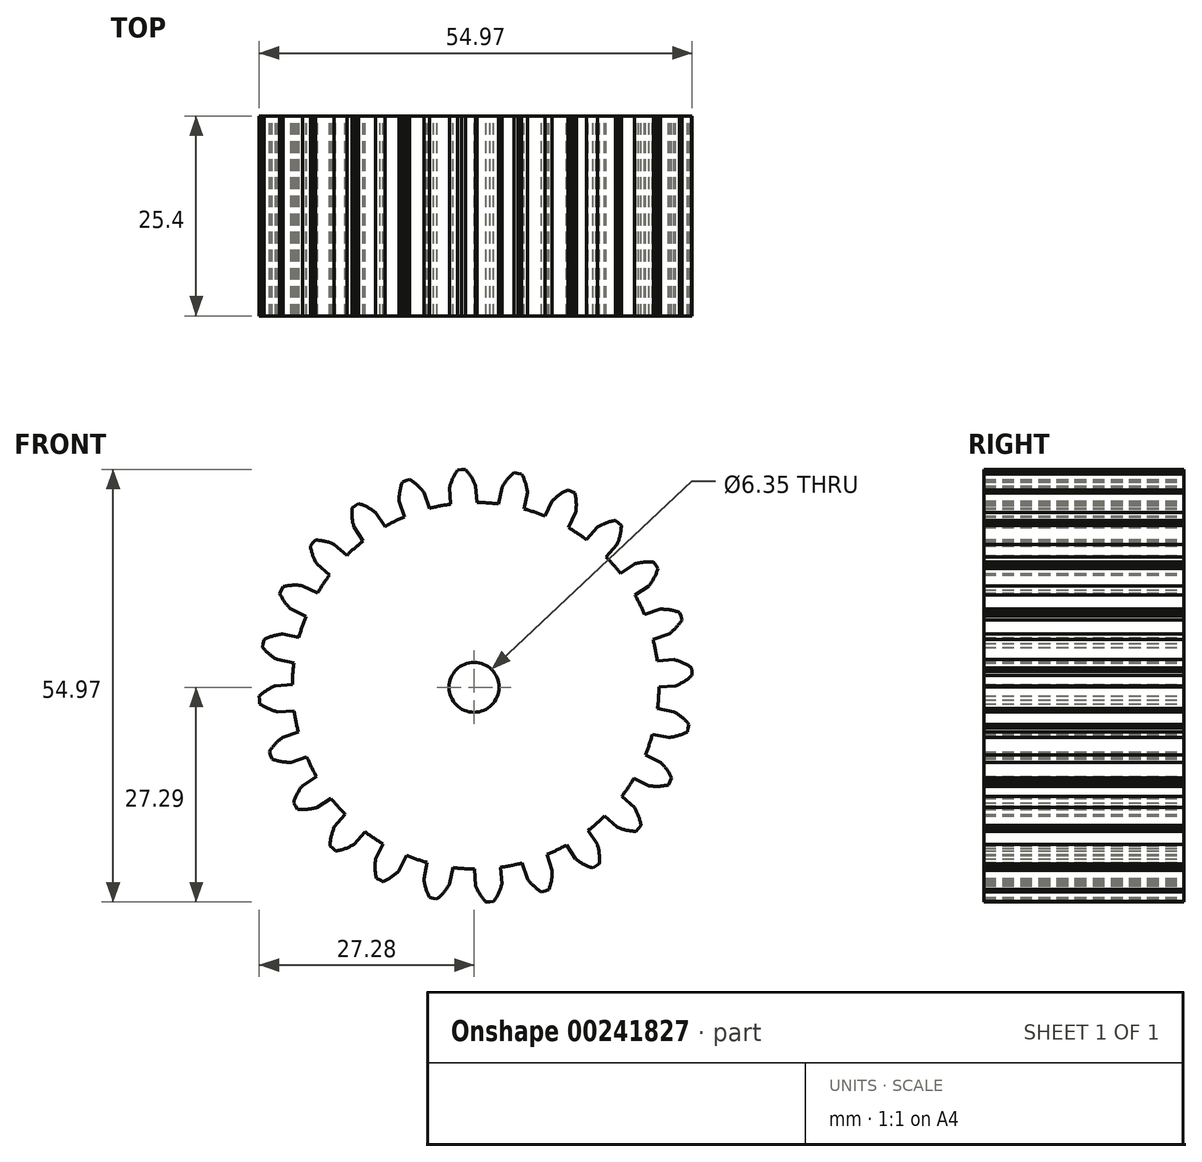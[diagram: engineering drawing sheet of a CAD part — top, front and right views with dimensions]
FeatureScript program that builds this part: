
annotation { "Feature Type Name" : "Feature", "Feature Type Description" : "" }
export const myFeature = defineFeature(function(context is Context, id is Id, definition is map)
    precondition{}
    {
        {
            var Q0;
            Q0=qCreatedBy(makeId("Front.planeOp"),FACE);
            var sketch = newSketch(context, id + "F0", { "sketchPlane" : qUnion([Q0])});
            skCircle(sketch, "E0", {"center": v(0.2, 0.2) * mm, "radius": 23.28 * mm});
            skArc(sketch, "E1.trimOffspring", {"start": v(0.2, 25.6) * mm, "mid": v(-0.35, 26.7) * mm, "end": v(-1.1, 27.68) * mm});
            skLineSegment(sketch, "E2", {"start": v(0.2, 25.6) * mm, "end": v(0.35, 23.48) * mm});
            skLineSegment(sketch, "E3", {"start": v(-1.1, 27.68) * mm, "end": v(-1.6, 27.66) * mm});
            skLineSegment(sketch, "E4.MirrorCS", {"start": v(-2.08, 27.61) * mm, "end": v(-1.6, 27.66) * mm});
            skArc(sketch, "E5.MirrorCS", {"start": v(-3.1, 25.38) * mm, "mid": v(-2.7, 26.55) * mm, "end": v(-2.08, 27.61) * mm});
            skLineSegment(sketch, "E6.MirrorCS", {"start": v(-3.1, 25.38) * mm, "end": v(-2.97, 23.26) * mm});
            skPoint(sketch, "E7.orphan", {"position": v(-2.8, 20.76) * mm});
            skPoint(sketch, "E8.orphan", {"position": v(0.51, 20.98) * mm});
            skLineSegment(sketch, "E9.1.0", {"start": v(-9.51, 23.66) * mm, "end": v(-8.83, 21.65) * mm});
            skArc(sketch, "E9.1.1", {"start": v(-9.51, 23.66) * mm, "mid": v(-9.42, 24.9) * mm, "end": v(-9.1, 26.09) * mm});
            skLineSegment(sketch, "E9.1.2", {"start": v(-9.1, 26.09) * mm, "end": v(-8.64, 26.25) * mm});
            skLineSegment(sketch, "E9.1.3", {"start": v(-8.17, 26.4) * mm, "end": v(-8.64, 26.25) * mm});
            skArc(sketch, "E9.1.4", {"start": v(-6.37, 24.73) * mm, "mid": v(-7.19, 25.65) * mm, "end": v(-8.17, 26.4) * mm});
            skLineSegment(sketch, "E9.1.5", {"start": v(-6.37, 24.73) * mm, "end": v(-5.68, 22.72) * mm});
            skLineSegment(sketch, "E9.2.0", {"start": v(-15.25, 20.35) * mm, "end": v(-14.08, 18.58) * mm});
            skArc(sketch, "E9.2.1", {"start": v(-15.25, 20.35) * mm, "mid": v(-15.49, 21.56) * mm, "end": v(-15.48, 22.8) * mm});
            skLineSegment(sketch, "E9.2.2", {"start": v(-15.48, 22.8) * mm, "end": v(-15.08, 23.08) * mm});
            skLineSegment(sketch, "E9.2.3", {"start": v(-14.67, 23.34) * mm, "end": v(-15.08, 23.08) * mm});
            skArc(sketch, "E9.2.4", {"start": v(-12.5, 22.2) * mm, "mid": v(-13.53, 22.87) * mm, "end": v(-14.67, 23.34) * mm});
            skLineSegment(sketch, "E9.2.5", {"start": v(-12.5, 22.2) * mm, "end": v(-11.31, 20.43) * mm});
            skLineSegment(sketch, "E9.3.0", {"start": v(-19.94, 15.66) * mm, "end": v(-18.35, 14.26) * mm});
            skArc(sketch, "E9.3.1", {"start": v(-19.94, 15.66) * mm, "mid": v(-20.48, 16.77) * mm, "end": v(-20.8, 17.97) * mm});
            skLineSegment(sketch, "E9.3.2", {"start": v(-20.8, 17.97) * mm, "end": v(-20.48, 18.34) * mm});
            skLineSegment(sketch, "E9.3.3", {"start": v(-20.16, 18.7) * mm, "end": v(-20.48, 18.34) * mm});
            skArc(sketch, "E9.3.4", {"start": v(-17.75, 18.15) * mm, "mid": v(-18.93, 18.54) * mm, "end": v(-20.16, 18.7) * mm});
            skLineSegment(sketch, "E9.3.5", {"start": v(-17.75, 18.15) * mm, "end": v(-16.16, 16.76) * mm});
            skLineSegment(sketch, "E9.4.0", {"start": v(-23.26, 9.91) * mm, "end": v(-21.36, 8.98) * mm});
            skArc(sketch, "E9.4.1", {"start": v(-23.26, 9.91) * mm, "mid": v(-24.07, 10.85) * mm, "end": v(-24.68, 11.93) * mm});
            skLineSegment(sketch, "E9.4.2", {"start": v(-24.68, 11.93) * mm, "end": v(-24.47, 12.37) * mm});
            skLineSegment(sketch, "E9.4.3", {"start": v(-24.25, 12.8) * mm, "end": v(-24.47, 12.37) * mm});
            skArc(sketch, "E9.4.4", {"start": v(-21.79, 12.9) * mm, "mid": v(-23.03, 12.97) * mm, "end": v(-24.25, 12.8) * mm});
            skLineSegment(sketch, "E9.4.5", {"start": v(-21.79, 12.9) * mm, "end": v(-19.89, 11.96) * mm});
            skLineSegment(sketch, "E9.5.0", {"start": v(-24.98, 3.5) * mm, "end": v(-22.9, 3.1) * mm});
            skArc(sketch, "E9.5.1", {"start": v(-24.98, 3.5) * mm, "mid": v(-26, 4.2) * mm, "end": v(-26.87, 5.08) * mm});
            skLineSegment(sketch, "E9.5.2", {"start": v(-26.87, 5.08) * mm, "end": v(-26.78, 5.56) * mm});
            skLineSegment(sketch, "E9.5.3", {"start": v(-26.68, 6.04) * mm, "end": v(-26.78, 5.56) * mm});
            skArc(sketch, "E9.5.4", {"start": v(-24.33, 6.77) * mm, "mid": v(-25.54, 6.52) * mm, "end": v(-26.68, 6.04) * mm});
            skLineSegment(sketch, "E9.5.5", {"start": v(-24.33, 6.77) * mm, "end": v(-22.25, 6.35) * mm});
            skLineSegment(sketch, "E9.6.0", {"start": v(-24.98, -3.12) * mm, "end": v(-22.86, -2.98) * mm});
            skArc(sketch, "E9.6.1", {"start": v(-24.98, -3.12) * mm, "mid": v(-26.14, -2.72) * mm, "end": v(-27.21, -2.1) * mm});
            skLineSegment(sketch, "E9.6.2", {"start": v(-27.21, -2.1) * mm, "end": v(-27.25, -1.6) * mm});
            skLineSegment(sketch, "E9.6.3", {"start": v(-27.28, -1.12) * mm, "end": v(-27.25, -1.6) * mm});
            skArc(sketch, "E9.6.4", {"start": v(-25.2, 0.2) * mm, "mid": v(-26.3, -0.36) * mm, "end": v(-27.28, -1.12) * mm});
            skLineSegment(sketch, "E9.6.5", {"start": v(-25.2, 0.2) * mm, "end": v(-23.07, 0.33) * mm});
            skLineSegment(sketch, "E9.7.0", {"start": v(-23.26, -9.53) * mm, "end": v(-21.25, -8.84) * mm});
            skArc(sketch, "E9.7.1", {"start": v(-23.26, -9.53) * mm, "mid": v(-24.5, -9.44) * mm, "end": v(-25.69, -9.11) * mm});
            skLineSegment(sketch, "E9.7.2", {"start": v(-25.69, -9.11) * mm, "end": v(-25.85, -8.65) * mm});
            skLineSegment(sketch, "E9.7.3", {"start": v(-26, -8.19) * mm, "end": v(-25.85, -8.65) * mm});
            skArc(sketch, "E9.7.4", {"start": v(-24.33, -6.38) * mm, "mid": v(-25.25, -7.2) * mm, "end": v(-26, -8.19) * mm});
            skLineSegment(sketch, "E9.7.5", {"start": v(-24.33, -6.38) * mm, "end": v(-22.32, -5.7) * mm});
            skLineSegment(sketch, "E9.8.0", {"start": v(-19.94, -15.27) * mm, "end": v(-18.18, -14.09) * mm});
            skArc(sketch, "E9.8.1", {"start": v(-19.94, -15.27) * mm, "mid": v(-21.16, -15.5) * mm, "end": v(-22.4, -15.5) * mm});
            skLineSegment(sketch, "E9.8.2", {"start": v(-22.4, -15.5) * mm, "end": v(-22.67, -15.1) * mm});
            skLineSegment(sketch, "E9.8.3", {"start": v(-22.94, -14.69) * mm, "end": v(-22.67, -15.1) * mm});
            skArc(sketch, "E9.8.4", {"start": v(-21.79, -12.5) * mm, "mid": v(-22.47, -13.54) * mm, "end": v(-22.94, -14.69) * mm});
            skLineSegment(sketch, "E9.8.5", {"start": v(-21.79, -12.5) * mm, "end": v(-20.02, -11.33) * mm});
            skLineSegment(sketch, "E9.9.0", {"start": v(-15.25, -19.96) * mm, "end": v(-13.86, -18.36) * mm});
            skArc(sketch, "E9.9.1", {"start": v(-15.25, -19.96) * mm, "mid": v(-16.37, -20.5) * mm, "end": v(-17.57, -20.81) * mm});
            skLineSegment(sketch, "E9.9.2", {"start": v(-17.57, -20.81) * mm, "end": v(-17.94, -20.5) * mm});
            skLineSegment(sketch, "E9.9.3", {"start": v(-18.3, -20.17) * mm, "end": v(-17.94, -20.5) * mm});
            skArc(sketch, "E9.9.4", {"start": v(-17.75, -17.77) * mm, "mid": v(-18.14, -18.94) * mm, "end": v(-18.3, -20.17) * mm});
            skLineSegment(sketch, "E9.9.5", {"start": v(-17.75, -17.77) * mm, "end": v(-16.35, -16.17) * mm});
            skLineSegment(sketch, "E9.10.0", {"start": v(-9.51, -23.27) * mm, "end": v(-8.57, -21.37) * mm});
            skArc(sketch, "E9.10.1", {"start": v(-9.51, -23.27) * mm, "mid": v(-10.45, -24.08) * mm, "end": v(-11.52, -24.7) * mm});
            skLineSegment(sketch, "E9.10.2", {"start": v(-11.52, -24.7) * mm, "end": v(-11.96, -24.49) * mm});
            skLineSegment(sketch, "E9.10.3", {"start": v(-12.4, -24.27) * mm, "end": v(-11.96, -24.49) * mm});
            skArc(sketch, "E9.10.4", {"start": v(-12.5, -21.8) * mm, "mid": v(-12.57, -23.04) * mm, "end": v(-12.4, -24.27) * mm});
            skLineSegment(sketch, "E9.10.5", {"start": v(-12.5, -21.8) * mm, "end": v(-11.55, -19.9) * mm});
            skLineSegment(sketch, "E9.11.0", {"start": v(-3.1, -24.99) * mm, "end": v(-2.7, -22.9) * mm});
            skArc(sketch, "E9.11.1", {"start": v(-3.1, -24.99) * mm, "mid": v(-3.8, -26.01) * mm, "end": v(-4.68, -26.88) * mm});
            skLineSegment(sketch, "E9.11.2", {"start": v(-4.68, -26.88) * mm, "end": v(-5.16, -26.8) * mm});
            skLineSegment(sketch, "E9.11.3", {"start": v(-5.64, -26.7) * mm, "end": v(-5.16, -26.8) * mm});
            skArc(sketch, "E9.11.4", {"start": v(-6.37, -24.34) * mm, "mid": v(-6.12, -25.55) * mm, "end": v(-5.64, -26.7) * mm});
            skLineSegment(sketch, "E9.11.5", {"start": v(-6.37, -24.34) * mm, "end": v(-5.95, -22.26) * mm});
            skLineSegment(sketch, "E9.12.0", {"start": v(3.52, -24.99) * mm, "end": v(3.38, -22.87) * mm});
            skArc(sketch, "E9.12.1", {"start": v(3.52, -24.99) * mm, "mid": v(3.12, -26.16) * mm, "end": v(2.5, -27.23) * mm});
            skLineSegment(sketch, "E9.12.2", {"start": v(2.5, -27.23) * mm, "end": v(2, -27.27) * mm});
            skLineSegment(sketch, "E9.12.3", {"start": v(1.52, -27.3) * mm, "end": v(2, -27.27) * mm});
            skArc(sketch, "E9.12.4", {"start": v(0.2, -25.2) * mm, "mid": v(0.76, -26.31) * mm, "end": v(1.52, -27.3) * mm});
            skLineSegment(sketch, "E9.12.5", {"start": v(0.2, -25.2) * mm, "end": v(0.07, -23.09) * mm});
            skLineSegment(sketch, "E9.13.0", {"start": v(9.93, -23.27) * mm, "end": v(9.25, -21.26) * mm});
            skArc(sketch, "E9.13.1", {"start": v(9.93, -23.27) * mm, "mid": v(9.84, -24.5) * mm, "end": v(9.51, -25.7) * mm});
            skLineSegment(sketch, "E9.13.2", {"start": v(9.51, -25.7) * mm, "end": v(9.05, -25.87) * mm});
            skLineSegment(sketch, "E9.13.3", {"start": v(8.6, -26.01) * mm, "end": v(9.05, -25.87) * mm});
            skArc(sketch, "E9.13.4", {"start": v(6.78, -24.34) * mm, "mid": v(7.6, -25.27) * mm, "end": v(8.6, -26.01) * mm});
            skLineSegment(sketch, "E9.13.5", {"start": v(6.78, -24.34) * mm, "end": v(6.1, -22.33) * mm});
            skLineSegment(sketch, "E9.14.0", {"start": v(15.67, -19.96) * mm, "end": v(14.5, -18.2) * mm});
            skArc(sketch, "E9.14.1", {"start": v(15.67, -19.96) * mm, "mid": v(15.9, -21.17) * mm, "end": v(15.9, -22.41) * mm});
            skLineSegment(sketch, "E9.14.2", {"start": v(15.9, -22.41) * mm, "end": v(15.5, -22.69) * mm});
            skLineSegment(sketch, "E9.14.3", {"start": v(15.09, -22.95) * mm, "end": v(15.5, -22.69) * mm});
            skArc(sketch, "E9.14.4", {"start": v(12.9, -21.8) * mm, "mid": v(13.94, -22.48) * mm, "end": v(15.09, -22.95) * mm});
            skLineSegment(sketch, "E9.14.5", {"start": v(12.9, -21.8) * mm, "end": v(11.73, -20.04) * mm});
            skLineSegment(sketch, "E9.15.0", {"start": v(20.36, -15.27) * mm, "end": v(18.76, -13.87) * mm});
            skArc(sketch, "E9.15.1", {"start": v(20.36, -15.27) * mm, "mid": v(20.9, -16.38) * mm, "end": v(21.21, -17.58) * mm});
            skLineSegment(sketch, "E9.15.2", {"start": v(21.21, -17.58) * mm, "end": v(20.9, -17.95) * mm});
            skLineSegment(sketch, "E9.15.3", {"start": v(20.57, -18.31) * mm, "end": v(20.9, -17.95) * mm});
            skArc(sketch, "E9.15.4", {"start": v(18.17, -17.77) * mm, "mid": v(19.34, -18.16) * mm, "end": v(20.57, -18.31) * mm});
            skLineSegment(sketch, "E9.15.5", {"start": v(18.17, -17.77) * mm, "end": v(16.57, -16.37) * mm});
            skLineSegment(sketch, "E9.16.0", {"start": v(23.67, -9.53) * mm, "end": v(21.77, -8.59) * mm});
            skArc(sketch, "E9.16.1", {"start": v(23.67, -9.53) * mm, "mid": v(24.48, -10.46) * mm, "end": v(25.1, -11.54) * mm});
            skLineSegment(sketch, "E9.16.2", {"start": v(25.1, -11.54) * mm, "end": v(24.89, -11.98) * mm});
            skLineSegment(sketch, "E9.16.3", {"start": v(24.67, -12.41) * mm, "end": v(24.89, -11.98) * mm});
            skArc(sketch, "E9.16.4", {"start": v(22.2, -12.5) * mm, "mid": v(23.44, -12.58) * mm, "end": v(24.67, -12.41) * mm});
            skLineSegment(sketch, "E9.16.5", {"start": v(22.2, -12.5) * mm, "end": v(20.3, -11.57) * mm});
            skLineSegment(sketch, "E9.17.0", {"start": v(25.4, -3.12) * mm, "end": v(23.3, -2.7) * mm});
            skArc(sketch, "E9.17.1", {"start": v(25.4, -3.12) * mm, "mid": v(26.42, -3.82) * mm, "end": v(27.29, -4.7) * mm});
            skLineSegment(sketch, "E9.17.2", {"start": v(27.29, -4.7) * mm, "end": v(27.2, -5.17) * mm});
            skLineSegment(sketch, "E9.17.3", {"start": v(27.1, -5.65) * mm, "end": v(27.2, -5.17) * mm});
            skArc(sketch, "E9.17.4", {"start": v(24.74, -6.38) * mm, "mid": v(25.95, -6.13) * mm, "end": v(27.1, -5.65) * mm});
            skLineSegment(sketch, "E9.17.5", {"start": v(24.74, -6.38) * mm, "end": v(22.66, -5.97) * mm});
            skLineSegment(sketch, "E9.18.0", {"start": v(25.4, 3.5) * mm, "end": v(23.27, 3.37) * mm});
            skArc(sketch, "E9.18.1", {"start": v(25.4, 3.5) * mm, "mid": v(26.56, 3.1) * mm, "end": v(27.63, 2.48) * mm});
            skLineSegment(sketch, "E9.18.2", {"start": v(27.63, 2.48) * mm, "end": v(27.67, 2) * mm});
            skLineSegment(sketch, "E9.18.3", {"start": v(27.7, 1.5) * mm, "end": v(27.67, 2) * mm});
            skArc(sketch, "E9.18.4", {"start": v(25.6, 0.2) * mm, "mid": v(26.71, 0.75) * mm, "end": v(27.7, 1.5) * mm});
            skLineSegment(sketch, "E9.18.5", {"start": v(25.6, 0.2) * mm, "end": v(23.5, 0.06) * mm});
            skLineSegment(sketch, "E9.19.0", {"start": v(23.67, 9.91) * mm, "end": v(21.66, 9.23) * mm});
            skArc(sketch, "E9.19.1", {"start": v(23.67, 9.91) * mm, "mid": v(24.9, 9.83) * mm, "end": v(26.1, 9.5) * mm});
            skLineSegment(sketch, "E9.19.2", {"start": v(26.1, 9.5) * mm, "end": v(26.27, 9.04) * mm});
            skLineSegment(sketch, "E9.19.3", {"start": v(26.42, 8.58) * mm, "end": v(26.27, 9.04) * mm});
            skArc(sketch, "E9.19.4", {"start": v(24.74, 6.77) * mm, "mid": v(25.67, 7.6) * mm, "end": v(26.42, 8.58) * mm});
            skLineSegment(sketch, "E9.19.5", {"start": v(24.74, 6.77) * mm, "end": v(22.73, 6.09) * mm});
            skLineSegment(sketch, "E9.20.0", {"start": v(20.36, 15.66) * mm, "end": v(18.6, 14.48) * mm});
            skArc(sketch, "E9.20.1", {"start": v(20.36, 15.66) * mm, "mid": v(21.57, 15.9) * mm, "end": v(22.81, 15.88) * mm});
            skLineSegment(sketch, "E9.20.2", {"start": v(22.81, 15.88) * mm, "end": v(23.09, 15.48) * mm});
            skLineSegment(sketch, "E9.20.3", {"start": v(23.35, 15.07) * mm, "end": v(23.09, 15.48) * mm});
            skArc(sketch, "E9.20.4", {"start": v(22.2, 12.9) * mm, "mid": v(22.89, 13.93) * mm, "end": v(23.35, 15.07) * mm});
            skLineSegment(sketch, "E9.20.5", {"start": v(22.2, 12.9) * mm, "end": v(20.44, 11.72) * mm});
            skLineSegment(sketch, "E9.21.0", {"start": v(15.67, 20.35) * mm, "end": v(14.27, 18.75) * mm});
            skArc(sketch, "E9.21.1", {"start": v(15.67, 20.35) * mm, "mid": v(16.78, 20.89) * mm, "end": v(17.98, 21.2) * mm});
            skLineSegment(sketch, "E9.21.2", {"start": v(17.98, 21.2) * mm, "end": v(18.35, 20.88) * mm});
            skLineSegment(sketch, "E9.21.3", {"start": v(18.71, 20.56) * mm, "end": v(18.35, 20.88) * mm});
            skArc(sketch, "E9.21.4", {"start": v(18.17, 18.15) * mm, "mid": v(18.56, 19.33) * mm, "end": v(18.71, 20.56) * mm});
            skLineSegment(sketch, "E9.21.5", {"start": v(18.17, 18.15) * mm, "end": v(16.77, 16.56) * mm});
            skLineSegment(sketch, "E9.22.0", {"start": v(9.93, 23.66) * mm, "end": v(8.99, 21.76) * mm});
            skArc(sketch, "E9.22.1", {"start": v(9.93, 23.66) * mm, "mid": v(10.86, 24.47) * mm, "end": v(11.94, 25.08) * mm});
            skLineSegment(sketch, "E9.22.2", {"start": v(11.94, 25.08) * mm, "end": v(12.38, 24.88) * mm});
            skLineSegment(sketch, "E9.22.3", {"start": v(12.81, 24.65) * mm, "end": v(12.38, 24.88) * mm});
            skArc(sketch, "E9.22.4", {"start": v(12.9, 22.2) * mm, "mid": v(12.98, 23.43) * mm, "end": v(12.81, 24.65) * mm});
            skLineSegment(sketch, "E9.22.5", {"start": v(12.9, 22.2) * mm, "end": v(11.97, 20.29) * mm});
            skLineSegment(sketch, "E9.23.0", {"start": v(3.52, 25.38) * mm, "end": v(3.1, 23.3) * mm});
            skArc(sketch, "E9.23.1", {"start": v(3.52, 25.38) * mm, "mid": v(4.22, 26.4) * mm, "end": v(5.1, 27.27) * mm});
            skLineSegment(sketch, "E9.23.2", {"start": v(5.1, 27.27) * mm, "end": v(5.58, 27.19) * mm});
            skLineSegment(sketch, "E9.23.3", {"start": v(6.05, 27.08) * mm, "end": v(5.58, 27.19) * mm});
            skArc(sketch, "E9.23.4", {"start": v(6.78, 24.73) * mm, "mid": v(6.53, 25.94) * mm, "end": v(6.05, 27.08) * mm});
            skLineSegment(sketch, "E9.23.5", {"start": v(6.78, 24.73) * mm, "end": v(6.37, 22.65) * mm});
            skCircle(sketch, "E10", {"center": v(0, 0) * mm, "radius": 3.18 * mm});
            skSolve(sketch);
        }
        {
            var Q0;
            Q0=makeQuery(id+"F0.imprint","IMPRINT",FACE,{"disambiguationData":[TD([[makeQuery(id+"F0.imprint","IMPRINT",EDGE,{"derivedFrom":sQuery(id+"F0.wireOp",EDGE,"E10")}),-1.0]])]});
            var Q1;
            {var subQ0=sQuery(id+"F0.wireOp",EDGE,"E9.4.0");Q1=makeQuery(id+"F0.imprint","IMPRINT",FACE,{"disambiguationData":[TD([[makeQuery(id+"F0.imprint","IMPRINT",EDGE,{"derivedFrom":subQ0}),1.0]])]});}
            var Q2;
            {var subQ0=sQuery(id+"F0.wireOp",EDGE,"E9.3.0");Q2=makeQuery(id+"F0.imprint","IMPRINT",FACE,{"disambiguationData":[TD([[makeQuery(id+"F0.imprint","IMPRINT",EDGE,{"derivedFrom":subQ0}),1.0]])]});}
            var Q3;
            {var subQ0=sQuery(id+"F0.wireOp",EDGE,"E9.2.0");Q3=makeQuery(id+"F0.imprint","IMPRINT",FACE,{"disambiguationData":[TD([[makeQuery(id+"F0.imprint","IMPRINT",EDGE,{"derivedFrom":subQ0}),1.0]])]});}
            var Q4;
            {var subQ0=sQuery(id+"F0.wireOp",EDGE,"E9.1.0");Q4=makeQuery(id+"F0.imprint","IMPRINT",FACE,{"disambiguationData":[TD([[makeQuery(id+"F0.imprint","IMPRINT",EDGE,{"derivedFrom":subQ0}),1.0]])]});}
            var Q5;
            Q5=makeQuery(id+"F0.imprint","IMPRINT",FACE,{"disambiguationData":[TD([[makeQuery(id+"F0.imprint","IMPRINT",EDGE,{"derivedFrom":sQuery(id+"F0.wireOp",EDGE,"E1.trimOffspring")}),1.0]])]});
            var Q6;
            {var subQ0=sQuery(id+"F0.wireOp",EDGE,"E9.23.0");Q6=makeQuery(id+"F0.imprint","IMPRINT",FACE,{"disambiguationData":[TD([[makeQuery(id+"F0.imprint","IMPRINT",EDGE,{"derivedFrom":subQ0}),1.0]])]});}
            var Q7;
            {var subQ0=sQuery(id+"F0.wireOp",EDGE,"E9.22.0");Q7=makeQuery(id+"F0.imprint","IMPRINT",FACE,{"disambiguationData":[TD([[makeQuery(id+"F0.imprint","IMPRINT",EDGE,{"derivedFrom":subQ0}),1.0]])]});}
            var Q8;
            {var subQ0=sQuery(id+"F0.wireOp",EDGE,"E9.21.0");Q8=makeQuery(id+"F0.imprint","IMPRINT",FACE,{"disambiguationData":[TD([[makeQuery(id+"F0.imprint","IMPRINT",EDGE,{"derivedFrom":subQ0}),1.0]])]});}
            var Q9;
            {var subQ0=sQuery(id+"F0.wireOp",EDGE,"E9.20.0");Q9=makeQuery(id+"F0.imprint","IMPRINT",FACE,{"disambiguationData":[TD([[makeQuery(id+"F0.imprint","IMPRINT",EDGE,{"derivedFrom":subQ0}),1.0]])]});}
            var Q10;
            {var subQ0=sQuery(id+"F0.wireOp",EDGE,"E9.19.0");Q10=makeQuery(id+"F0.imprint","IMPRINT",FACE,{"disambiguationData":[TD([[makeQuery(id+"F0.imprint","IMPRINT",EDGE,{"derivedFrom":subQ0}),1.0]])]});}
            var Q11;
            {var subQ0=sQuery(id+"F0.wireOp",EDGE,"E9.18.0");Q11=makeQuery(id+"F0.imprint","IMPRINT",FACE,{"disambiguationData":[TD([[makeQuery(id+"F0.imprint","IMPRINT",EDGE,{"derivedFrom":subQ0}),1.0]])]});}
            var Q12;
            {var subQ0=sQuery(id+"F0.wireOp",EDGE,"E9.17.0");Q12=makeQuery(id+"F0.imprint","IMPRINT",FACE,{"disambiguationData":[TD([[makeQuery(id+"F0.imprint","IMPRINT",EDGE,{"derivedFrom":subQ0}),1.0]])]});}
            var Q13;
            {var subQ0=sQuery(id+"F0.wireOp",EDGE,"E9.16.0");Q13=makeQuery(id+"F0.imprint","IMPRINT",FACE,{"disambiguationData":[TD([[makeQuery(id+"F0.imprint","IMPRINT",EDGE,{"derivedFrom":subQ0}),1.0]])]});}
            var Q14;
            {var subQ0=sQuery(id+"F0.wireOp",EDGE,"E9.15.0");Q14=makeQuery(id+"F0.imprint","IMPRINT",FACE,{"disambiguationData":[TD([[makeQuery(id+"F0.imprint","IMPRINT",EDGE,{"derivedFrom":subQ0}),1.0]])]});}
            var Q15;
            {var subQ1=sQuery(id+"F0.wireOp",EDGE,"E9.14.0");Q15=makeQuery(id+"F0.imprint","IMPRINT",FACE,{"disambiguationData":[TD([[makeQuery(id+"F0.imprint","IMPRINT",EDGE,{"derivedFrom":subQ1}),1.0]])]});}
            var Q16;
            {var subQ0=sQuery(id+"F0.wireOp",EDGE,"E9.13.0");Q16=makeQuery(id+"F0.imprint","IMPRINT",FACE,{"disambiguationData":[TD([[makeQuery(id+"F0.imprint","IMPRINT",EDGE,{"derivedFrom":subQ0}),1.0]])]});}
            var Q17;
            {var subQ0=sQuery(id+"F0.wireOp",EDGE,"E9.12.0");Q17=makeQuery(id+"F0.imprint","IMPRINT",FACE,{"disambiguationData":[TD([[makeQuery(id+"F0.imprint","IMPRINT",EDGE,{"derivedFrom":subQ0}),1.0]])]});}
            var Q18;
            {var subQ0=sQuery(id+"F0.wireOp",EDGE,"E9.11.0");Q18=makeQuery(id+"F0.imprint","IMPRINT",FACE,{"disambiguationData":[TD([[makeQuery(id+"F0.imprint","IMPRINT",EDGE,{"derivedFrom":subQ0}),1.0]])]});}
            var Q19;
            {var subQ0=sQuery(id+"F0.wireOp",EDGE,"E9.10.0");Q19=makeQuery(id+"F0.imprint","IMPRINT",FACE,{"disambiguationData":[TD([[makeQuery(id+"F0.imprint","IMPRINT",EDGE,{"derivedFrom":subQ0}),1.0]])]});}
            var Q20;
            {var subQ1=sQuery(id+"F0.wireOp",EDGE,"E9.9.0");Q20=makeQuery(id+"F0.imprint","IMPRINT",FACE,{"disambiguationData":[TD([[makeQuery(id+"F0.imprint","IMPRINT",EDGE,{"derivedFrom":subQ1}),1.0]])]});}
            var Q21;
            {var subQ0=sQuery(id+"F0.wireOp",EDGE,"E9.8.0");Q21=makeQuery(id+"F0.imprint","IMPRINT",FACE,{"disambiguationData":[TD([[makeQuery(id+"F0.imprint","IMPRINT",EDGE,{"derivedFrom":subQ0}),1.0]])]});}
            var Q22;
            {var subQ0=sQuery(id+"F0.wireOp",EDGE,"E9.7.0");Q22=makeQuery(id+"F0.imprint","IMPRINT",FACE,{"disambiguationData":[TD([[makeQuery(id+"F0.imprint","IMPRINT",EDGE,{"derivedFrom":subQ0}),1.0]])]});}
            var Q23;
            {var subQ0=sQuery(id+"F0.wireOp",EDGE,"E9.6.0");Q23=makeQuery(id+"F0.imprint","IMPRINT",FACE,{"disambiguationData":[TD([[makeQuery(id+"F0.imprint","IMPRINT",EDGE,{"derivedFrom":subQ0}),1.0]])]});}
            var Q24;
            {var subQ0=sQuery(id+"F0.wireOp",EDGE,"E9.5.0");Q24=makeQuery(id+"F0.imprint","IMPRINT",FACE,{"disambiguationData":[TD([[makeQuery(id+"F0.imprint","IMPRINT",EDGE,{"derivedFrom":subQ0}),1.0]])]});}
            extrude(context, id + "F1", {"entities" : qUnion([Q0, Q1, Q2, Q3, Q4, Q5, Q6, Q7, Q8, Q9, Q10, Q11, Q12, Q13, Q14, Q15, Q16, Q17, Q18, Q19, Q20, Q21, Q22, Q23, Q24]), "depth" : 25.4 * mm});
        }
    });
